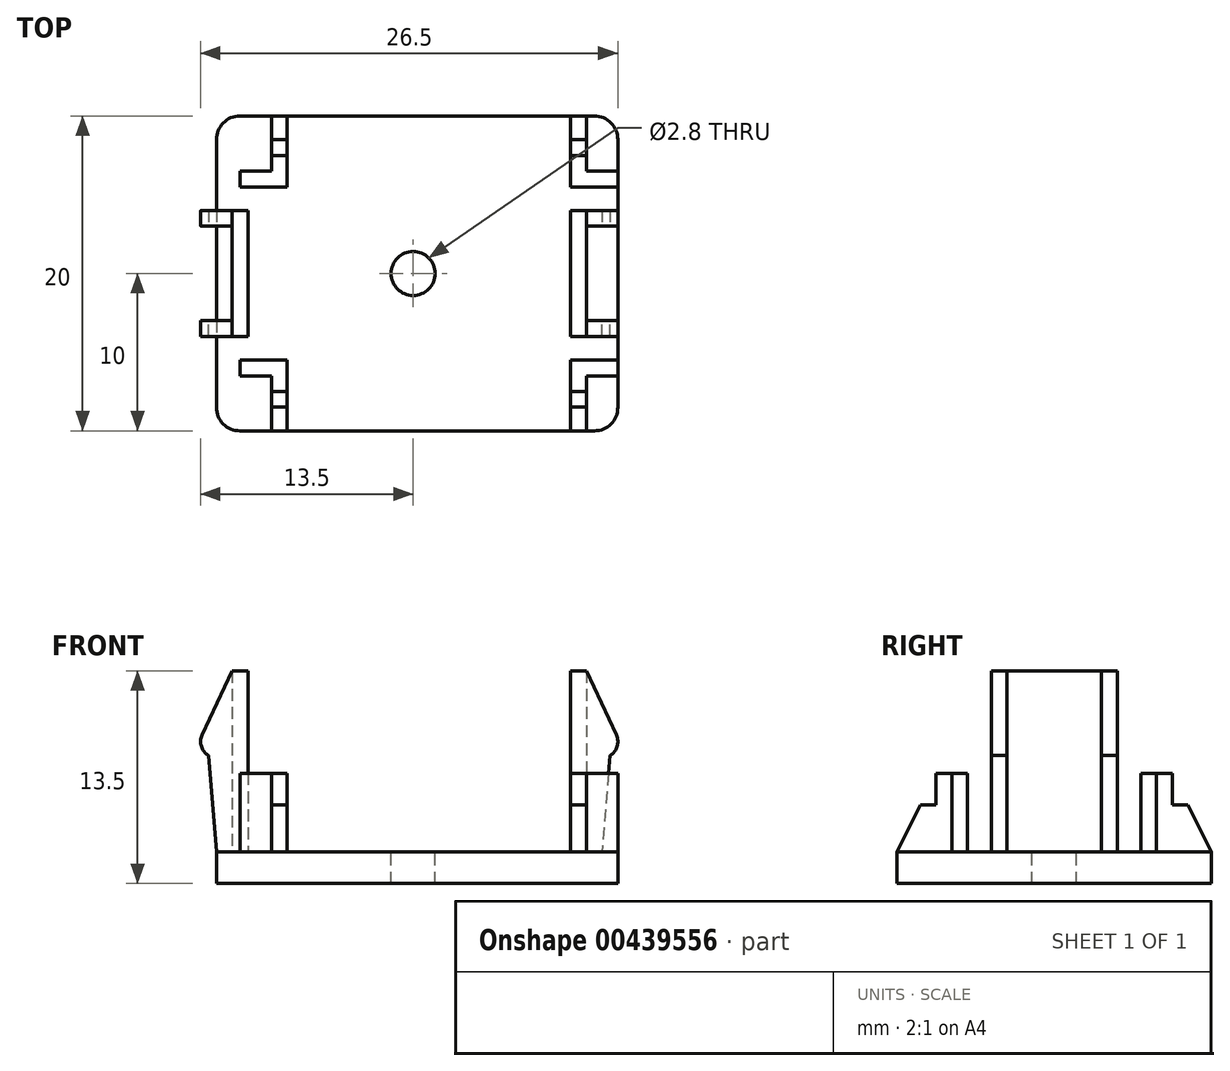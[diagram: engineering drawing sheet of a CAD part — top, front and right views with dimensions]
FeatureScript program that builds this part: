
annotation { "Feature Type Name" : "Feature", "Feature Type Description" : "" }
export const myFeature = defineFeature(function(context is Context, id is Id, definition is map)
    precondition{}
    {
        {
            var Q0;
            Q0=qCreatedBy(makeId("Top.planeOp"),FACE);
            var sketch = newSketch(context, id + "F0", { "sketchPlane" : qUnion([Q0])});
            skLineSegment(sketch, "E0", {"start": v(-7.5, 10) * mm, "end": v(-7.5, 5.5) * mm});
            skLineSegment(sketch, "E1", {"start": v(-7.5, 5.5) * mm, "end": v(-10.5, 5.5) * mm});
            skLineSegment(sketch, "E2", {"start": v(-10.5, 5.5) * mm, "end": v(-10.5, 6.5) * mm});
            skLineSegment(sketch, "E3", {"start": v(-10.5, 6.5) * mm, "end": v(-8.5, 6.5) * mm});
            skLineSegment(sketch, "E4", {"start": v(-8.5, 6.5) * mm, "end": v(-8.5, 10) * mm});
            skLineSegment(sketch, "E5", {"start": v(-8.5, 10) * mm, "end": v(-7.5, 10) * mm});
            skLineSegment(sketch, "E6", {"start": v(-13, 4) * mm, "end": v(-10, 4) * mm});
            skLineSegment(sketch, "E7", {"start": v(-10, 4) * mm, "end": v(-10, 0) * mm});
            skLineSegment(sketch, "E8", {"start": v(-10, 0) * mm, "end": v(-11, 0) * mm});
            skLineSegment(sketch, "E9", {"start": v(-11, 0) * mm, "end": v(-11, 3) * mm});
            skLineSegment(sketch, "E10", {"start": v(-11, 3) * mm, "end": v(-13, 3) * mm});
            skLineSegment(sketch, "E11", {"start": v(-13, 3) * mm, "end": v(-13, 4) * mm});
            skLineSegment(sketch, "E12", {"start": v(10.5, 10) * mm, "end": v(10.5, 5.5) * mm});
            skPoint(sketch, "E12.startSnap0", {"position": v(-8, 10) * mm});
            skLineSegment(sketch, "E13", {"start": v(10.5, 5.5) * mm, "end": v(13.5, 5.5) * mm});
            skLineSegment(sketch, "E14", {"start": v(13.5, 5.5) * mm, "end": v(13.5, 6.5) * mm});
            skLineSegment(sketch, "E15", {"start": v(13.5, 6.5) * mm, "end": v(11.5, 6.5) * mm});
            skLineSegment(sketch, "E16", {"start": v(11.5, 6.5) * mm, "end": v(11.5, 10) * mm});
            skLineSegment(sketch, "E17", {"start": v(11.5, 10) * mm, "end": v(10.5, 10) * mm});
            skLineSegment(sketch, "E18", {"start": v(10.5, 4) * mm, "end": v(10.5, 0) * mm});
            skLineSegment(sketch, "E19", {"start": v(10.5, 0) * mm, "end": v(11.5, 0) * mm});
            skLineSegment(sketch, "E20", {"start": v(11.5, 0) * mm, "end": v(11.5, 3) * mm});
            skLineSegment(sketch, "E21", {"start": v(11.5, 3) * mm, "end": v(13.5, 3) * mm});
            skLineSegment(sketch, "E22", {"start": v(13.5, 3) * mm, "end": v(13.5, 4) * mm});
            skLineSegment(sketch, "E23", {"start": v(13.5, 4) * mm, "end": v(10.5, 4) * mm});
            skSolve(sketch);
        }
        {
            var Q0;
            Q0=makeQuery(id+"F0.imprint","IMPRINT",FACE,{"disambiguationData":[TD([[makeQuery(id+"F0.imprint","IMPRINT",EDGE,{"derivedFrom":sQuery(id+"F0.wireOp",EDGE,"E0")}),-1.0]])]});
            var Q1;
            Q1=makeQuery(id+"F0.imprint","IMPRINT",FACE,{"disambiguationData":[TD([[makeQuery(id+"F0.imprint","IMPRINT",EDGE,{"derivedFrom":sQuery(id+"F0.wireOp",EDGE,"E6")}),-1.0]])]});
            var Q2;
            Q2=makeQuery(id+"F0.imprint","IMPRINT",FACE,{"disambiguationData":[TD([[makeQuery(id+"F0.imprint","IMPRINT",EDGE,{"derivedFrom":sQuery(id+"F0.wireOp",EDGE,"E12")}),1.0]])]});
            var Q3;
            Q3=makeQuery(id+"F0.imprint","IMPRINT",FACE,{"disambiguationData":[TD([[makeQuery(id+"F0.imprint","IMPRINT",EDGE,{"derivedFrom":sQuery(id+"F0.wireOp",EDGE,"E18")}),1.0]])]});
            extrude(context, id + "F1", {"entities" : qUnion([Q0, Q1, Q2, Q3]), "depth" : 11.5 * mm});
        }
        {
            var Q0;
            Q0=makeQuery(id+"F1.opExtrude","SWEPT_FACE",FACE,{"disambiguationData":[OSD([sQuery(id+"F0.wireOp",EDGE,"E10")])]});
            var sketch = newSketch(context, id + "F2", { "sketchPlane" : qUnion([Q0])});
            skArc(sketch, "E24", {"start": v(-12.9, 7.42) * mm, "mid": v(-12.95, 6.7) * mm, "end": v(-12.5, 6.13) * mm});
            skArc(sketch, "E25", {"start": v(13.4, 7.42) * mm, "mid": v(13.45, 6.7) * mm, "end": v(13, 6.13) * mm});
            skLineSegment(sketch, "E26", {"start": v(-12, 0) * mm, "end": v(-12.5, 6.13) * mm});
            skLineSegment(sketch, "E27", {"start": v(-12, 0) * mm, "end": v(-13, 0) * mm});
            skLineSegment(sketch, "E28", {"start": v(-13, 0) * mm, "end": v(-13, 7) * mm});
            skLineSegment(sketch, "E29", {"start": v(-11, 11.5) * mm, "end": v(-12.9, 7.42) * mm});
            skLineSegment(sketch, "E30", {"start": v(-11, 11.5) * mm, "end": v(-13, 11.5) * mm});
            skLineSegment(sketch, "E31", {"start": v(-13, 11.5) * mm, "end": v(-13, 7) * mm});
            skLineSegment(sketch, "E32", {"start": v(12.5, 0) * mm, "end": v(13, 6.13) * mm});
            skLineSegment(sketch, "E33", {"start": v(12.5, 0) * mm, "end": v(13.5, 0) * mm});
            skLineSegment(sketch, "E34", {"start": v(13.5, 0) * mm, "end": v(13.5, 7) * mm});
            skLineSegment(sketch, "E35", {"start": v(11.5, 11.5) * mm, "end": v(13.4, 7.42) * mm});
            skLineSegment(sketch, "E36", {"start": v(11.5, 11.5) * mm, "end": v(13.5, 11.5) * mm});
            skLineSegment(sketch, "E37", {"start": v(13.5, 11.5) * mm, "end": v(13.5, 7) * mm});
            skSolve(sketch);
        }
        {
            var Q0;
            {var subQ0=sQuery(id+"F2.wireOp",EDGE,"E29");Q0=makeQuery(id+"F2.imprint","IMPRINT",FACE,{"disambiguationData":[TD([[makeQuery(id+"F2.imprint","IMPRINT",EDGE,{"derivedFrom":subQ0}),-1.0]])]});}
            var Q1;
            {var subQ0=sQuery(id+"F2.wireOp",EDGE,"E26");Q1=makeQuery(id+"F2.imprint","IMPRINT",FACE,{"disambiguationData":[TD([[makeQuery(id+"F2.imprint","IMPRINT",EDGE,{"derivedFrom":subQ0}),1.0]])]});}
            var Q2;
            {var subQ0=sQuery(id+"F2.wireOp",EDGE,"E35");Q2=makeQuery(id+"F2.imprint","IMPRINT",FACE,{"disambiguationData":[TD([[makeQuery(id+"F2.imprint","IMPRINT",EDGE,{"derivedFrom":subQ0}),1.0]])]});}
            var Q3;
            {var subQ0=sQuery(id+"F2.wireOp",EDGE,"E32");Q3=makeQuery(id+"F2.imprint","IMPRINT",FACE,{"disambiguationData":[TD([[makeQuery(id+"F2.imprint","IMPRINT",EDGE,{"derivedFrom":subQ0}),-1.0]])]});}
            extrude(context, id + "F3", {"entities" : qUnion([Q0, Q1, Q2, Q3]), "operationType" : NewBodyOperationType.REMOVE, "endBound" : BoundingType.UP_TO_NEXT, "oppositeDirection" : true, "depth" : 25 * mm});
        }
        {
            var Q0;
            Q0=makeQuery(id+"F1.opExtrude","SWEPT_BODY",BODY,{"disambiguationData":[OSD([sQuery(id+"F0.wireOp",EDGE,"E6"),sQuery(id+"F0.wireOp",EDGE,"E7"),sQuery(id+"F0.wireOp",EDGE,"E8"),sQuery(id+"F0.wireOp",EDGE,"E9"),sQuery(id+"F0.wireOp",EDGE,"E10"),sQuery(id+"F0.wireOp",EDGE,"E11")])]});
            var Q1;
            Q1=makeQuery(id+"F1.opExtrude","SWEPT_BODY",BODY,{"disambiguationData":[OSD([sQuery(id+"F0.wireOp",EDGE,"E18"),sQuery(id+"F0.wireOp",EDGE,"E19"),sQuery(id+"F0.wireOp",EDGE,"E20"),sQuery(id+"F0.wireOp",EDGE,"E21"),sQuery(id+"F0.wireOp",EDGE,"E22"),sQuery(id+"F0.wireOp",EDGE,"E23")])]});
            var Q2;
            Q2=makeQuery(id+"F1.opExtrude","SWEPT_BODY",BODY,{"disambiguationData":[OSD([sQuery(id+"F0.wireOp",EDGE,"E12"),sQuery(id+"F0.wireOp",EDGE,"E13"),sQuery(id+"F0.wireOp",EDGE,"E14"),sQuery(id+"F0.wireOp",EDGE,"E15"),sQuery(id+"F0.wireOp",EDGE,"E16"),sQuery(id+"F0.wireOp",EDGE,"E17")])]});
            var Q3;
            Q3=makeQuery(id+"F1.opExtrude","SWEPT_BODY",BODY,{"disambiguationData":[OSD([sQuery(id+"F0.wireOp",EDGE,"E0"),sQuery(id+"F0.wireOp",EDGE,"E1"),sQuery(id+"F0.wireOp",EDGE,"E2"),sQuery(id+"F0.wireOp",EDGE,"E3"),sQuery(id+"F0.wireOp",EDGE,"E4"),sQuery(id+"F0.wireOp",EDGE,"E5")])]});
            var Q4;
            Q4=qCreatedBy(makeId("Front.planeOp"),FACE);
            mirror(context, id + "F4", {"operationType" : NewBodyOperationType.ADD, "entities" : qUnion([Q0, Q1, Q2, Q3]), "mirrorPlane" : qUnion([Q4])});
        }
        {
            var Q0;
            Q0=makeQuery(id+"F1.opExtrude","SWEPT_FACE",FACE,{"disambiguationData":[OSD([sQuery(id+"F0.wireOp",EDGE,"E4")])]});
            var sketch = newSketch(context, id + "F5", { "sketchPlane" : qUnion([Q0])});
            skLineSegment(sketch, "E38.bottom", {"start": v(-10, 11.5) * mm, "end": v(-5.5, 11.5) * mm});
            skLineSegment(sketch, "E38.top", {"start": v(-10, 5) * mm, "end": v(-5.5, 5) * mm});
            skLineSegment(sketch, "E38.left", {"start": v(-10, 11.5) * mm, "end": v(-10, 5) * mm});
            skLineSegment(sketch, "E38.right", {"start": v(-5.5, 11.5) * mm, "end": v(-5.5, 5) * mm});
            skLineSegment(sketch, "E39.bottom", {"start": v(10, 11.5) * mm, "end": v(5.5, 11.5) * mm});
            skLineSegment(sketch, "E39.top", {"start": v(10, 5) * mm, "end": v(5.5, 5) * mm});
            skLineSegment(sketch, "E39.left", {"start": v(10, 11.5) * mm, "end": v(10, 5) * mm});
            skLineSegment(sketch, "E39.right", {"start": v(5.5, 11.5) * mm, "end": v(5.5, 5) * mm});
            skSolve(sketch);
        }
        {
            var Q0;
            Q0 = qSketchRegion(id + "F5", true);
            extrude(context, id + "F6", {"entities" : qUnion([Q0]), "operationType" : NewBodyOperationType.REMOVE, "endBound" : BoundingType.SYMMETRIC, "oppositeDirection" : true, "depth" : 56.26 * mm});
        }
        {
            var Q0;
            Q0=makeQuery(id+"F1.opExtrude","SWEPT_FACE",FACE,{"disambiguationData":[OSD([sQuery(id+"F0.wireOp",EDGE,"E4")])]});
            var sketch = newSketch(context, id + "F7", { "sketchPlane" : qUnion([Q0])});
            skLineSegment(sketch, "E40", {"start": v(-10, 0) * mm, "end": v(-8.5, 3) * mm});
            skLineSegment(sketch, "E41", {"start": v(-8.5, 3) * mm, "end": v(-7.5, 3) * mm});
            skLineSegment(sketch, "E42", {"start": v(-7.5, 3) * mm, "end": v(-7.5, 5) * mm});
            skLineSegment(sketch, "E43", {"start": v(-7.5, 5) * mm, "end": v(-10, 5) * mm});
            skLineSegment(sketch, "E44", {"start": v(-10, 5) * mm, "end": v(-10, 0) * mm});
            skSolve(sketch);
        }
        {
            var Q0;
            Q0=makeQuery(id+"F7.imprint","IMPRINT",FACE,{"disambiguationData":[TD([[makeQuery(id+"F7.imprint","IMPRINT",EDGE,{"derivedFrom":sQuery(id+"F7.wireOp",EDGE,"E40")}),1.0]])]});
            extrude(context, id + "F8", {"entities" : qUnion([Q0]), "operationType" : NewBodyOperationType.REMOVE, "endBound" : BoundingType.THROUGH_ALL, "oppositeDirection" : true, "depth" : 25 * mm});
        }
        {
            var Q0;
            Q0=makeQuery(id+"F4.opPattern","COPY",FACE,{"derivedFrom":makeQuery(id+"F1.opExtrude","SWEPT_FACE",FACE,{"disambiguationData":[OSD([sQuery(id+"F0.wireOp",EDGE,"E4")])]}),"instanceName":"1"});
            var sketch = newSketch(context, id + "F9", { "sketchPlane" : qUnion([Q0])});
            skLineSegment(sketch, "E45", {"start": v(10, 0) * mm, "end": v(8.5, 3) * mm});
            skLineSegment(sketch, "E46", {"start": v(8.5, 3) * mm, "end": v(7.5, 3) * mm});
            skLineSegment(sketch, "E47", {"start": v(7.5, 3) * mm, "end": v(7.5, 5) * mm});
            skLineSegment(sketch, "E48", {"start": v(7.5, 5) * mm, "end": v(10, 5) * mm});
            skLineSegment(sketch, "E49", {"start": v(10, 5) * mm, "end": v(10, 0) * mm});
            skSolve(sketch);
        }
        {
            var Q0;
            Q0=makeQuery(id+"F9.imprint","IMPRINT",FACE,{"disambiguationData":[TD([[makeQuery(id+"F9.imprint","IMPRINT",EDGE,{"derivedFrom":sQuery(id+"F9.wireOp",EDGE,"E45")}),-1.0]])]});
            extrude(context, id + "F10", {"entities" : qUnion([Q0]), "operationType" : NewBodyOperationType.REMOVE, "endBound" : BoundingType.THROUGH_ALL, "oppositeDirection" : true, "depth" : 25 * mm});
        }
        {
            var Q0;
            Q0=qCreatedBy(makeId("Top.planeOp"),FACE);
            var sketch = newSketch(context, id + "F11", { "sketchPlane" : qUnion([Q0])});
            skLineSegment(sketch, "E50.bottom", {"start": v(-10.5, 10) * mm, "end": v(12, 10) * mm});
            skLineSegment(sketch, "E50.top", {"start": v(-10.5, -10) * mm, "end": v(12, -10) * mm});
            skLineSegment(sketch, "E50.left", {"start": v(-12, 8.5) * mm, "end": v(-12, -8.5) * mm});
            skLineSegment(sketch, "E50.right", {"start": v(13.5, 8.5) * mm, "end": v(13.5, -8.5) * mm});
            skPoint(sketch, "E51.visualSharp", {"position": v(-12, 10) * mm});
            skArc(sketch, "E51.filletArc", {"start": v(-10.5, 10) * mm, "mid": v(-11.56, 9.56) * mm, "end": v(-12, 8.5) * mm});
            skPoint(sketch, "E52.visualSharp", {"position": v(13.5, 10) * mm});
            skArc(sketch, "E52.filletArc", {"start": v(13.5, 8.5) * mm, "mid": v(13.06, 9.56) * mm, "end": v(12, 10) * mm});
            skPoint(sketch, "E53.visualSharp", {"position": v(13.5, -10) * mm});
            skArc(sketch, "E53.filletArc", {"start": v(12, -10) * mm, "mid": v(13.06, -9.56) * mm, "end": v(13.5, -8.5) * mm});
            skPoint(sketch, "E54.visualSharp", {"position": v(-12, -10) * mm});
            skArc(sketch, "E54.filletArc", {"start": v(-12, -8.5) * mm, "mid": v(-11.56, -9.56) * mm, "end": v(-10.5, -10) * mm});
            skCircle(sketch, "E55", {"center": v(0.5, 0) * mm, "radius": 1.4 * mm});
            skSolve(sketch);
        }
        {
            var Q0;
            Q0=makeQuery(id+"F11.imprint","IMPRINT",FACE,{"disambiguationData":[TD([[makeQuery(id+"F11.imprint","IMPRINT",EDGE,{"derivedFrom":sQuery(id+"F11.wireOp",EDGE,"E50.bottom")}),-1.0]])]});
            extrude(context, id + "F12", {"entities" : qUnion([Q0]), "oppositeDirection" : true, "depth" : 2 * mm});
        }
    });
